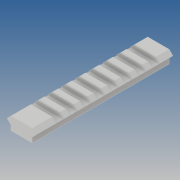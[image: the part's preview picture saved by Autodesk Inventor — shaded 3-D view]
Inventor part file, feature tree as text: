
AUTODESK INVENTOR PART (.ipt)
format: ipt  version: 2019 (Build 230136000, 136)  size: 136,704 bytes
history: native  units: mm
features: extrude x2, sketch x2, pattern_linear x1, other x1
ambient origin geometry x8: Origin, YZ Plane, XZ Plane, XY Plane, X Axis, Y Axis, Z Axis, Center Point
bodies: Solide1 (feature_tree)
feature tree (6):
  extrude  "Extrusion1"  Depth=15.67mm
  extrude  "Extrusion2"  TaperAngle=45.0deg  [1 undecoded]
  pattern_linear  "Réseau rectangulaire1"  Spacing1=45.0deg  [1 undecoded]
  sketch  "Esquisse1"
  sketch  "Esquisse3"
  other  "Projeter les arêtes coupées1"
note: 2 required parameter values undecoded (feature->parameter linkage not recoverable at this tier; creation-order binding heuristic only, values carry confidence <= 0.55)
